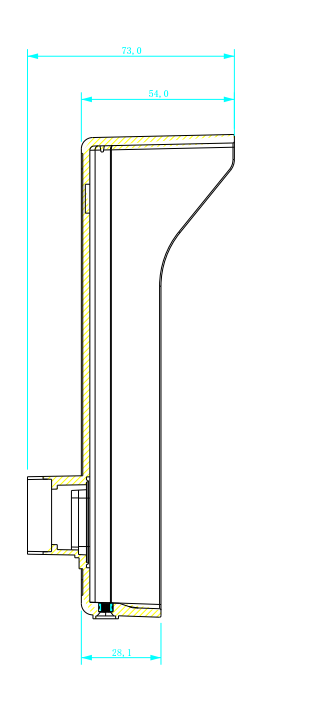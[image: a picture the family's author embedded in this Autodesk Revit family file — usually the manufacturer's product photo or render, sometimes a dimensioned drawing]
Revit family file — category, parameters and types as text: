
# Revit family: AU-04LAF + SP-AU
name_source: partatom
category: Устройства связи
units: mm (PartAtom-declared; Revit-internal decimal feet)

## family parameters
Всегда вертикально = Нет
На основе рабочей плоскости = Да
Общий = Да
При загрузке вырезать с полостями = Нет
Размер круглого соединителя = Использовать диаметр
Сохранять ориентацию аннотаций = Нет
Тип детали = Нормальный
Точка расчета площади = Нет

## types (1)
- AU-04LAF + SP-AU
    ADSK_URL документации изделия = https://cdn.bas-ip.com
    ADSK_URL страницы изделия = https://bas-ip.com          https://bas-ip.com
    ADSK_Версия Revit = Revit 2020
    ADSK_Единица измерения = шт
    ADSK_Завод-изготовитель = BAS-IP
    ADSK_Классификация нагрузок = Внутренний монитор индивидуальный
    ADSK_Количество фаз = 1
    ADSK_Коэффициент мощности = 0.9
    ADSK_Марка = AU-04LAF + SP-AU
    ADSK_Наименование = Внутренний монитор индивидуальный с аудиотрубкой AU-04LAF + SP-AU
    ADSK_Наименование краткое = AU-04LAF + SP-AU
    ADSK_Напряжение = 12 В
    ADSK_Номинальная мощность = 3 Вт
    ADSK_Полная мощность = 3 В·А
    ADSK_Размер_Длина = 185 мм
    ADSK_Размер_Толщина = 30 мм
    ADSK_Размер_Ширина = 135 мм
    BIM library = https://bimlib.ru
    URL = https://www.bas-ip.ru
    Аудиотрубка SP-AU = 60 ×185 мм
    Встроенная камера = Нет
    Габаритные размеры внутреннего монитора с SP-AU = 195×185×30 мм
    Голосовая почта = Нет
    Группа модели = Внутренний монитор индивидуальный
    Дисплей = 4,3-дюймовый TFT LCD, сенсорный, емкостный
    Дополнительно = Подключение кнопки звонка; SIP P2P; Управляемый выход при поступлении входящего звонка
    Изготовитель = BAS-IP
    Изображение типоразмера = <Нет>
    Интерфейс = Мультиязычный, графический
    Количество IP-камер = до 8 камер
    Количество индивидуальных вызывных панелей = до 9 панелей
    Количество многоквартирных вызывных панелей = до 9 панелей
    Корпус = пластик
    Модуль Wi-Fi = Да
    Мощность = 6 Вт, в режиме ожидания — 2,5 Вт
    Обновление программного обеспечения = через Ethernet
    Общий вес = 0,61 кг
    Описание = Самый бюджетный IP видеодомофон в линейке BAS-IP. Одной из особенностей AU-04LAF является возможность подключения дополнительной трубки SP-AU. Это решение идеально подходит для тех, кто желает конфиденциальности в разговорах. Управление домофоном возможно с помощью механических клавиш и сенсорного экрана. Классический черный и белый цвет корпуса подойдут для любого стиля интерьера. Мониторы AU-04LAF не поддерживают работу с вызывными панелями второй версии (v2).
    Отметка по умолчанию = 0 мм
    Память = Запись фото во внутреннюю память
    Поддержка получения сообщений = Да
    Подключение дополнительных мониторов = До 5 мониторов
    Просмотр IP-камер в режиме ожидания = Да
    Рабочая влажность = 20–80 %
    Рабочая температура = -10 – +55 °С
    Размеры внутреннего монитора = 135×185×30 мм
    Размеры коробки = 233×168,5×65 мм
    Разрешение экрана = 480×272
    Режим фоторамки = Нет
    Сигнализация = 4 входа для датчиков
    Сценарии = Нет
    Тип домофона = Видеодомофон
    Тип установки = Настенный монтаж
    Управление домашней автоматикой = свет, шторы, лифт
    Цветовое решение = белый, черный
    Электропитание = PoE, +12 В постоянного тока (+11%-6%)
